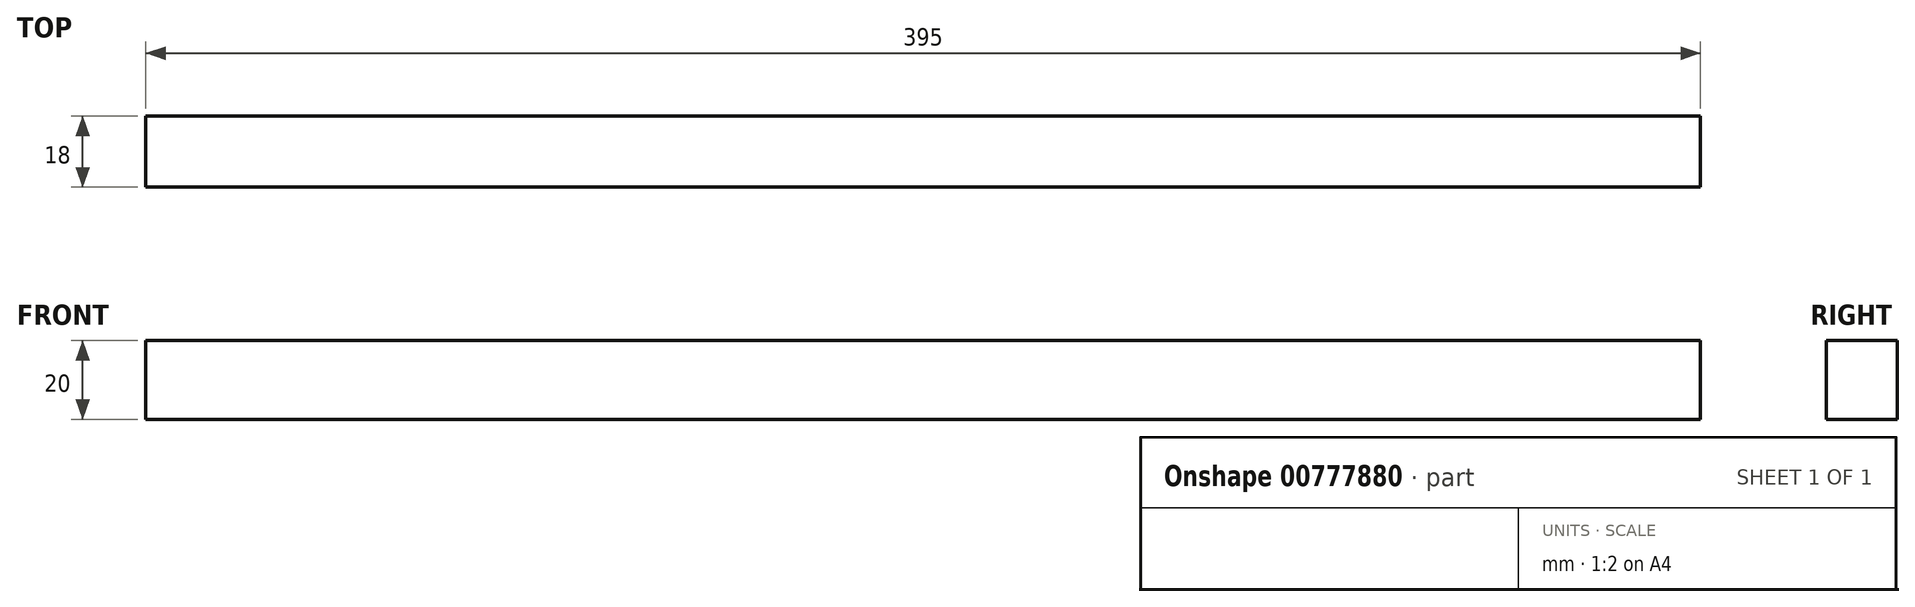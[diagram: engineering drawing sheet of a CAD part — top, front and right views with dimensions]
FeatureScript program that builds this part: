
annotation { "Feature Type Name" : "Feature", "Feature Type Description" : "" }
export const myFeature = defineFeature(function(context is Context, id is Id, definition is map)
    precondition{}
    {
        {
            var Q0;
            Q0=qCreatedBy(makeId("Top.planeOp"),FACE);
            var sketch = newSketch(context, id + "F0", { "sketchPlane" : qUnion([Q0])});
            skLineSegment(sketch, "E0.bottom", {"start": v(-197.5, 9) * mm, "end": v(197.5, 9) * mm});
            skLineSegment(sketch, "E0.top", {"start": v(-197.5, -9) * mm, "end": v(197.5, -9) * mm});
            skLineSegment(sketch, "E0.left", {"start": v(-197.5, 9) * mm, "end": v(-197.5, -9) * mm});
            skLineSegment(sketch, "E0.right", {"start": v(197.5, 9) * mm, "end": v(197.5, -9) * mm});
            skSolve(sketch);
        }
        {
            var Q0;
            Q0 = qSketchRegion(id + "F0", true);
            extrude(context, id + "F1", {"entities" : qUnion([Q0]), "endBound" : BoundingType.SYMMETRIC, "depth" : 20 * mm, "offsetDistance" : 25 * mm});
        }
    });
